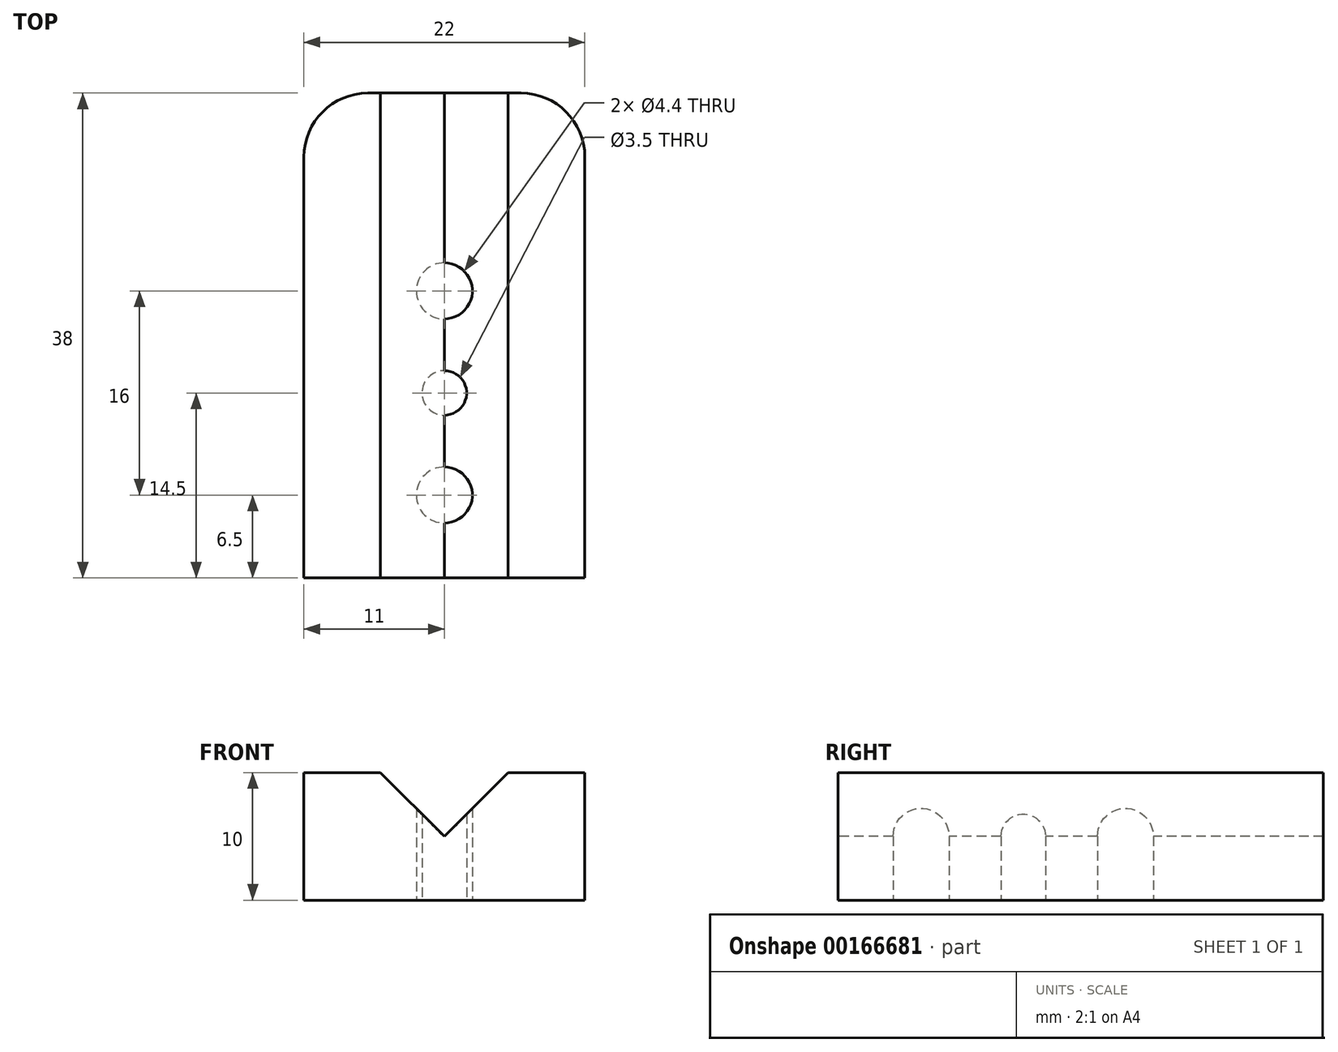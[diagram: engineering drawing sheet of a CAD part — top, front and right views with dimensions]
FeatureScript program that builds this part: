
annotation { "Feature Type Name" : "Feature", "Feature Type Description" : "" }
export const myFeature = defineFeature(function(context is Context, id is Id, definition is map)
    precondition{}
    {
        {
            var Q0;
            Q0=qCreatedBy(makeId("Front.planeOp"),FACE);
            var sketch = newSketch(context, id + "F0", { "sketchPlane" : qUnion([Q0])});
            skLineSegment(sketch, "E0", {"start": v(-11, 0) * mm, "end": v(11, 0) * mm});
            skLineSegment(sketch, "E1", {"start": v(11, 0) * mm, "end": v(11, 10) * mm});
            skLineSegment(sketch, "E2", {"start": v(11, 10) * mm, "end": v(5, 10) * mm});
            skLineSegment(sketch, "E3", {"start": v(5, 10) * mm, "end": v(0, 5) * mm});
            skLineSegment(sketch, "E4", {"start": v(0, 5) * mm, "end": v(-5, 10) * mm});
            skLineSegment(sketch, "E5", {"start": v(-5, 10) * mm, "end": v(-11, 10) * mm});
            skLineSegment(sketch, "E6", {"start": v(-11, 10) * mm, "end": v(-11, 0) * mm});
            skSolve(sketch);
        }
        {
            var Q0;
            Q0 = qSketchRegion(id + "F0", true);
            extrude(context, id + "F1", {"entities" : qUnion([Q0]), "oppositeDirection" : true, "depth" : 38 * mm});
        }
        {
            var Q0;
            Q0=makeQuery(id+"F1.opExtrude","CAP_EDGE",EDGE,{"disambiguationData":[OSD([sQuery(id+"F0.wireOp",EDGE,"E1")])],"isStart":false});
            var Q1;
            Q1=makeQuery(id+"F1.opExtrude","CAP_EDGE",EDGE,{"disambiguationData":[OSD([sQuery(id+"F0.wireOp",EDGE,"E6")])],"isStart":false});
            fillet(context, id + "F2", {"entities" : qUnion([Q0, Q1]), "radius" : 5 * mm, "tangentPropagation" : true, "allowEdgeOverflow" : false});
        }
        {
            var Q0;
            Q0=qCreatedBy(makeId("Top.planeOp"),FACE);
            var sketch = newSketch(context, id + "F3", { "sketchPlane" : qUnion([Q0])});
            skCircle(sketch, "E7", {"center": v(0, 6.5) * mm, "radius": 2.2 * mm});
            skCircle(sketch, "E8", {"center": v(0, 22.5) * mm, "radius": 2.2 * mm});
            skCircle(sketch, "E9", {"center": v(0, 14.5) * mm, "radius": 1.75 * mm});
            skSolve(sketch);
        }
        {
            var Q0;
            Q0 = qSketchRegion(id + "F3", true);
            extrude(context, id + "F4", {"entities" : qUnion([Q0]), "operationType" : NewBodyOperationType.REMOVE, "endBound" : BoundingType.THROUGH_ALL, "depth" : 25 * mm});
        }
    });
